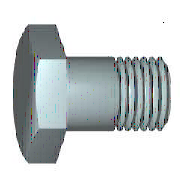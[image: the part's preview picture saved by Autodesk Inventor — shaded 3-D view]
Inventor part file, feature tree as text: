
AUTODESK INVENTOR PART (.ipt)
format: ipt  version: 2019 (Build 230136000, 136)  size: 196,608 bytes
history: native  units: mm (DEFAULTED — no unit token found)
features: sketch x3, extrude x1, chamfer x1, plane x1
ambient origin geometry x7: Origin, YZ Plane, XZ Plane, X Axis, Y Axis, Z Axis, Center Point
bodies: Solid1 (feature_tree), Body (feature_tree)
feature tree (6):
  extrude  "Head"  Depth=32.6mm
  chamfer  "Chamfer1"  Distance=3.0mm
  plane  "Work Plane1"
  sketch  "Sketch1"  dims[d0=35.0mm d1=32.6mm]
  sketch  "Sketch2"  dims[d2=5.0mm]
  sketch  "Sketch4"  dims[d12=90.0deg d3=3.0mm d4=0.0mm d5=30.0deg d21=90.0deg d6=0.49076mm d7=0.49086mm d8=0.0mm d9=0.5001mm d10=8.0mm d11=8.0mm d13=0.49086mm d14=5.0mm d15=32.6mm d16=0.0mm d19=8.0mm d55=45.0deg d57=0.0mm d58=0.0mm]
